# Revit family: BuzziFalls Revised
name_source: partatom
category: Furniture
revit_build: Autodesk Revit 2018 (Build: 20190510_1515(x64)
units: mm (PartAtom-declared; Revit-internal decimal feet)

## family parameters
Always vertical = Yes
Cut with Voids When Loaded = No
OmniClass Number = 23.40.20.00
OmniClass Title = General Furniture and Specialties
Room Calculation Point = No
Shared = No
Work Plane-Based = No

## types (16) — shared parameters
Baseplate = <By Category>
Frame = <By Category>
Panel Back = <By Category>
Panel Front = <By Category>

## per-type parameters (varying)
| type | Alhahmbra | Birch | Cubes | Dots | Grid | Leaves | Orient | Palms | Parrots | Pebbles | Plain | Rain | Royal | Squares | Stars | Tropics |
| Alhahmbra | Yes | No | No | No | No | No | No | No | No | No | No | No | No | No | No | No |
| Birch | No | Yes | No | No | No | No | No | No | No | No | No | No | No | No | No | No |
| Cubes | No | No | Yes | No | No | No | No | No | No | No | No | No | No | No | No | No |
| Dots | No | No | No | Yes | No | No | No | No | No | No | No | No | No | No | No | No |
| Grid | No | No | No | No | Yes | No | No | No | No | No | No | No | No | No | No | No |
| Leaves | No | No | No | No | No | Yes | No | No | No | No | No | No | No | No | No | No |
| Orient | No | No | No | No | No | No | Yes | No | No | No | No | No | No | No | No | No |
| Palms | No | No | No | No | No | No | No | Yes | No | No | No | No | No | No | No | No |
| Parrots | No | No | No | No | No | No | No | No | Yes | No | No | No | No | No | No | No |
| Pebbles | No | No | No | No | No | No | No | No | No | Yes | No | No | No | No | No | No |
| Plain | No | No | No | No | No | No | No | No | No | No | Yes | No | No | No | No | No |
| Rain | No | No | No | No | No | No | No | No | No | No | No | Yes | No | No | No | No |
| Royal | No | No | No | No | No | No | No | No | No | No | No | No | Yes | No | No | No |
| Squares | No | No | No | No | No | No | No | No | No | No | No | No | No | Yes | No | No |
| Stars | No | No | No | No | No | No | No | No | No | No | No | No | No | No | Yes | No |
| Tropics | No | No | No | No | No | No | No | No | No | No | No | No | No | No | No | Yes |

## geometry (parser evidence)
native form markers: Sweep x2
no freeform markers — native parametric forms only
